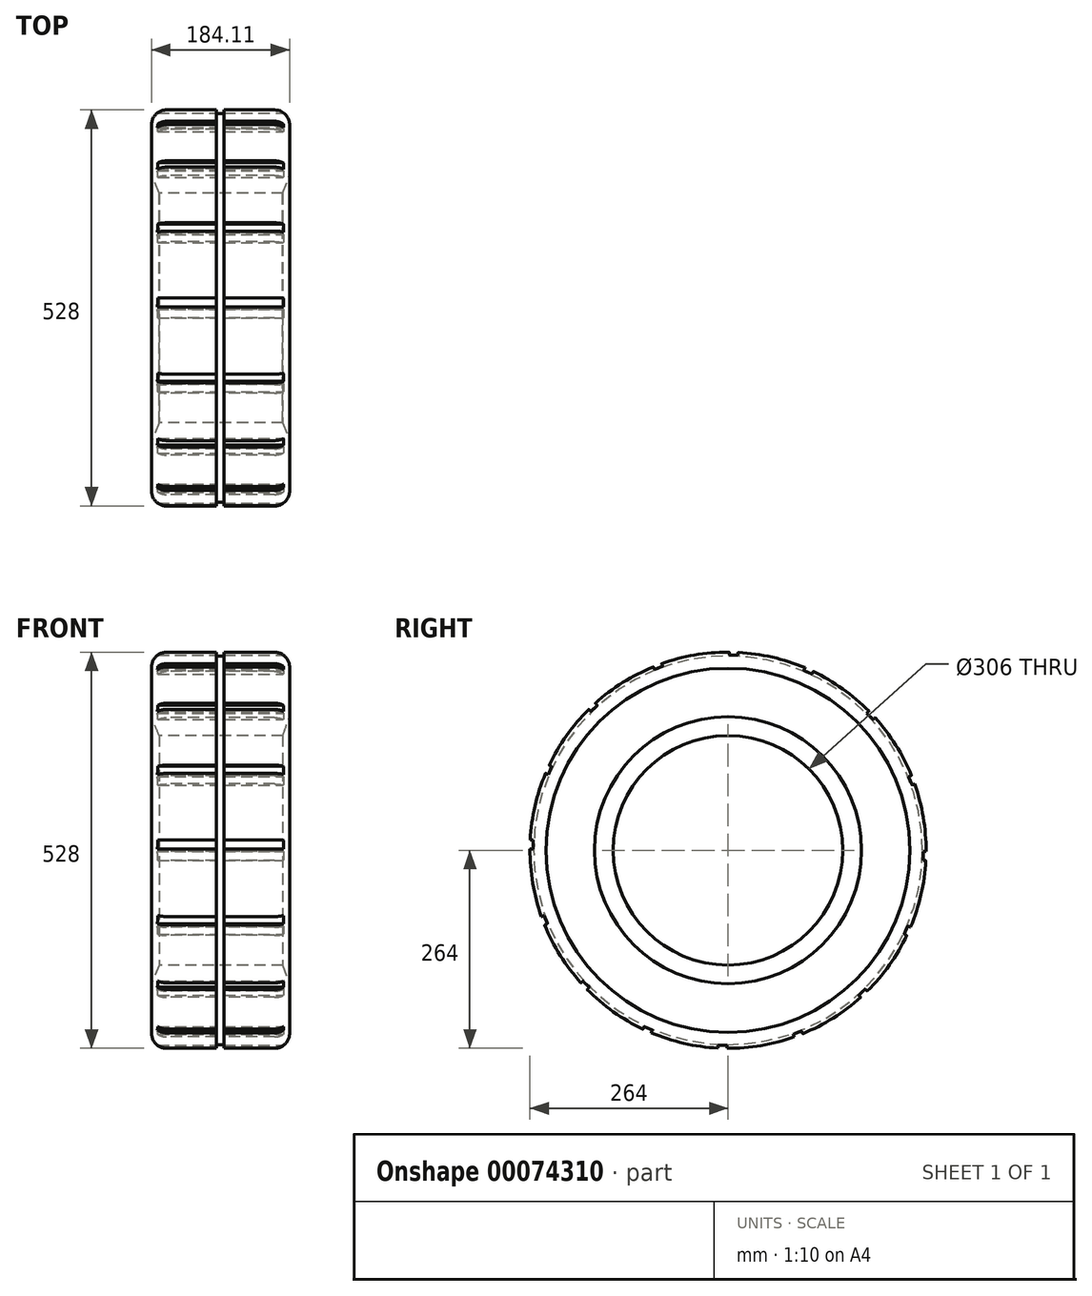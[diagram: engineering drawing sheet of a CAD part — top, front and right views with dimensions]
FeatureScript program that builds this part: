
annotation { "Feature Type Name" : "Feature", "Feature Type Description" : "" }
export const myFeature = defineFeature(function(context is Context, id is Id, definition is map)
    precondition{}
    {
        {
            var Q0;
            Q0=qCreatedBy(makeId("Front.planeOp"),FACE);
            var sketch = newSketch(context, id + "F0", { "sketchPlane" : qUnion([Q0])});
            skLineSegment(sketch, "E0", {"start": v(-276.1, 0) * mm, "end": v(269.09, 0) * mm, "construction": true});
            skLineSegment(sketch, "E1", {"start": v(-82.5, 153) * mm, "end": v(82.5, 153) * mm});
            skLineSegment(sketch, "E2", {"start": v(0, 0) * mm, "end": v(92.5, 153) * mm, "construction": true});
            skLineSegment(sketch, "E3", {"start": v(-72.5, 264) * mm, "end": v(-5.94, 264) * mm});
            skLineSegment(sketch, "E4", {"start": v(-92.5, 244) * mm, "end": v(-92.5, 178) * mm});
            skPoint(sketch, "E5.visualSharp", {"position": v(-92.5, 264) * mm});
            skArc(sketch, "E5.filletArc", {"start": v(-72.5, 264) * mm, "mid": v(-86.64, 258.14) * mm, "end": v(-92.5, 244) * mm});
            skPoint(sketch, "E6.visualSharp", {"position": v(92.5, 264) * mm});
            skArc(sketch, "E6.filletArc", {"start": v(91.56, 242.63) * mm, "mid": v(86.23, 257.65) * mm, "end": v(71.61, 264) * mm});
            skLineSegment(sketch, "E7", {"start": v(-82.5, 153) * mm, "end": v(-92.5, 178) * mm, "construction": true});
            skPoint(sketch, "E8.orphan", {"position": v(-92.5, 153) * mm});
            skPoint(sketch, "E9.end.orphan", {"position": v(91.56, 178) * mm});
            skLineSegment(sketch, "E10", {"start": v(91.56, 242.63) * mm, "end": v(91.56, 178) * mm});
            skLineSegment(sketch, "E11", {"start": v(91.56, 178) * mm, "end": v(82.5, 153) * mm});
            skLineSegment(sketch, "E12", {"start": v(-92.5, 178) * mm, "end": v(-82.5, 153) * mm});
            skLineSegment(sketch, "E13.top", {"start": v(4.06, 259) * mm, "end": v(-5.94, 259) * mm});
            skLineSegment(sketch, "E13.left", {"start": v(4.06, 264) * mm, "end": v(4.06, 259) * mm});
            skLineSegment(sketch, "E13.right", {"start": v(-5.94, 264) * mm, "end": v(-5.94, 259) * mm});
            skLineSegment(sketch, "E14.trimOffspring", {"start": v(4.06, 264) * mm, "end": v(71.61, 264) * mm});
            skSolve(sketch);
        }
        {
            var Q0;
            Q0=qSketchRegion(id+"F0",true);
            var Q1;
            Q1=sQuery(id+"F0.wireOp",EDGE,"E0");
            revolve(context, id + "F1", {"entities" : qUnion([Q0]), "axis" : qUnion([Q1]), "revolveType" : RevolveType.FULL});
        }
        {
            var Q0;
            Q0=qCreatedBy(makeId("Top.planeOp"),FACE);
            cPlane(context, id + "F2", {"entities" : qUnion([Q0]), "cplaneType" : CPlaneType.OFFSET, "offset" : 260 * mm, "width" : 150 * mm, "height" : 150 * mm});
        }
        {
            var Q0;
            Q0=qCreatedBy(id+"F2.planeOp",FACE);
            var sketch = newSketch(context, id + "F3", { "sketchPlane" : qUnion([Q0])});
            skLineSegment(sketch, "E15.bottom", {"start": v(-111.23, 13.57) * mm, "end": v(113, 13.57) * mm});
            skLineSegment(sketch, "E15.top", {"start": v(-111.23, 1.57) * mm, "end": v(113, 1.57) * mm});
            skLineSegment(sketch, "E15.left", {"start": v(-111.23, 13.57) * mm, "end": v(-111.23, 1.57) * mm});
            skLineSegment(sketch, "E15.right", {"start": v(113, 13.57) * mm, "end": v(113, 1.57) * mm});
            skSolve(sketch);
        }
        {
            var Q0;
            Q0=qSketchRegion(id+"F3",true);
            extrude(context, id + "F4", {"entities" : qUnion([Q0]), "operationType" : NewBodyOperationType.REMOVE, "depth" : 25 * mm});
        }
        {
            var Q0;
            Q0=makeQuery(id+"F1.opRevolve","SWEPT_BODY",BODY,{"disambiguationData":[OSD([sQuery(id+"F0.wireOp",EDGE,"E1"),sQuery(id+"F0.wireOp",EDGE,"E3"),sQuery(id+"F0.wireOp",EDGE,"E4"),sQuery(id+"F0.wireOp",EDGE,"E5.filletArc"),sQuery(id+"F0.wireOp",EDGE,"E6.filletArc"),sQuery(id+"F0.wireOp",EDGE,"E10"),sQuery(id+"F0.wireOp",EDGE,"E11"),sQuery(id+"F0.wireOp",EDGE,"E12"),sQuery(id+"F0.wireOp",EDGE,"E13.top"),sQuery(id+"F0.wireOp",EDGE,"E13.left"),sQuery(id+"F0.wireOp",EDGE,"E13.right"),sQuery(id+"F0.wireOp",EDGE,"E14.trimOffspring")])]});
            transform(context, id + "F5", {"entities" : qUnion([Q0]), "transformType" : TransformType.TRANSLATION_3D, "dx" : 0 * mm, "dy" : 0 * mm, "dz" : 0 * mm, "makeCopy" : true});
        }
        {
            var Q0;
            {var subQ0=sQuery(id+"F3.wireOp",EDGE,"E15.top");Q0=makeQuery(id+"F4.boolean.opBoolean","COPY",FACE,{"disambiguationData":[TD([makeQuery(id+"F1.opRevolve","SWEPT_FACE",FACE,{"disambiguationData":[OSD([sQuery(id+"F0.wireOp",EDGE,"E6.filletArc")])]})])],"derivedFrom":makeQuery(id+"F4.opExtrude","SWEPT_FACE",FACE,{"disambiguationData":[OSD([subQ0])]})});}
            var Q1;
            {var subQ0=sQuery(id+"F3.wireOp",EDGE,"E15.bottom");var subQ1=sQuery(id+"F3.wireOp",EDGE,"E15.top");Q1=makeQuery(id+"F4.boolean.opBoolean","COPY",FACE,{"disambiguationData":[TD([makeQuery(id+"F1.opRevolve","SWEPT_FACE",FACE,{"disambiguationData":[OSD([sQuery(id+"F0.wireOp",EDGE,"E6.filletArc")])]})])],"derivedFrom":makeQuery(id+"F4.opExtrude","CAP_FACE",FACE,{"disambiguationData":[OSD([subQ0,subQ1,sQuery(id+"F3.wireOp",EDGE,"E15.left"),sQuery(id+"F3.wireOp",EDGE,"E15.right")])],"isStart":true})});}
            var Q2;
            {var subQ0=sQuery(id+"F3.wireOp",EDGE,"E15.bottom");Q2=makeQuery(id+"F4.boolean.opBoolean","COPY",FACE,{"disambiguationData":[TD([makeQuery(id+"F1.opRevolve","SWEPT_FACE",FACE,{"disambiguationData":[OSD([sQuery(id+"F0.wireOp",EDGE,"E6.filletArc")])]})])],"derivedFrom":makeQuery(id+"F4.opExtrude","SWEPT_FACE",FACE,{"disambiguationData":[OSD([subQ0])]})});}
            var Q3;
            Q3=makeQuery(id+"F1.opRevolve","SWEPT_EDGE",EDGE,{"disambiguationData":[OSD([sQuery(id+"F0.wireOp",EDGE,"E4"),sQuery(id+"F0.wireOp",EDGE,"E5.filletArc")])]});
            circularPattern(context, id + "F6", {"faces" : qUnion([Q0, Q1, Q2]), "axis" : qUnion([Q3]), "angle" : 360 * degree, "instanceCount" : 16, "equalSpace" : true, "patternType" : PatternType.FACE});
        }
        {
            var Q0;
            Q0=makeQuery(id+"F5.opPattern","COPY",BODY,{"derivedFrom":makeQuery(id+"F1.opRevolve","SWEPT_BODY",BODY,{"disambiguationData":[OSD([sQuery(id+"F0.wireOp",EDGE,"E1"),sQuery(id+"F0.wireOp",EDGE,"E3"),sQuery(id+"F0.wireOp",EDGE,"E4"),sQuery(id+"F0.wireOp",EDGE,"E5.filletArc"),sQuery(id+"F0.wireOp",EDGE,"E6.filletArc"),sQuery(id+"F0.wireOp",EDGE,"E10"),sQuery(id+"F0.wireOp",EDGE,"E11"),sQuery(id+"F0.wireOp",EDGE,"E12"),sQuery(id+"F0.wireOp",EDGE,"E13.top"),sQuery(id+"F0.wireOp",EDGE,"E13.left"),sQuery(id+"F0.wireOp",EDGE,"E13.right"),sQuery(id+"F0.wireOp",EDGE,"E14.trimOffspring")])]}),"instanceName":"1"});
            deleteBodies(context, id + "F7", {"entities" : qUnion([Q0])});
        }
        {
            var Q0;
            {var subQ0=sQuery(id+"F3.wireOp",EDGE,"E15.bottom");var subQ1=sQuery(id+"F3.wireOp",EDGE,"E15.top");Q0=makeQuery(id+"F4.boolean.opBoolean","COPY",FACE,{"disambiguationData":[TD([makeQuery(id+"F1.opRevolve","SWEPT_FACE",FACE,{"disambiguationData":[OSD([sQuery(id+"F0.wireOp",EDGE,"E5.filletArc")])]})])],"derivedFrom":makeQuery(id+"F4.opExtrude","CAP_FACE",FACE,{"disambiguationData":[OSD([subQ0,subQ1,sQuery(id+"F3.wireOp",EDGE,"E15.left"),sQuery(id+"F3.wireOp",EDGE,"E15.right")])],"isStart":true})});}
            var Q1;
            {var subQ0=sQuery(id+"F3.wireOp",EDGE,"E15.top");Q1=makeQuery(id+"F4.boolean.opBoolean","COPY",FACE,{"disambiguationData":[TD([makeQuery(id+"F1.opRevolve","SWEPT_FACE",FACE,{"disambiguationData":[OSD([sQuery(id+"F0.wireOp",EDGE,"E3")])]})])],"derivedFrom":makeQuery(id+"F4.opExtrude","SWEPT_FACE",FACE,{"disambiguationData":[OSD([subQ0])]})});}
            var Q2;
            {var subQ0=sQuery(id+"F3.wireOp",EDGE,"E15.bottom");Q2=makeQuery(id+"F4.boolean.opBoolean","COPY",FACE,{"disambiguationData":[TD([makeQuery(id+"F1.opRevolve","SWEPT_FACE",FACE,{"disambiguationData":[OSD([sQuery(id+"F0.wireOp",EDGE,"E3")])]})])],"derivedFrom":makeQuery(id+"F4.opExtrude","SWEPT_FACE",FACE,{"disambiguationData":[OSD([subQ0])]})});}
            var Q3;
            Q3=makeQuery(id+"F1.opRevolve","SWEPT_EDGE",EDGE,{"disambiguationData":[OSD([sQuery(id+"F0.wireOp",EDGE,"E4"),sQuery(id+"F0.wireOp",EDGE,"E12")])]});
            circularPattern(context, id + "F8", {"faces" : qUnion([Q0, Q1, Q2]), "axis" : qUnion([Q3]), "angle" : 360 * degree, "instanceCount" : 16, "equalSpace" : true, "patternType" : PatternType.FACE});
        }
    });
